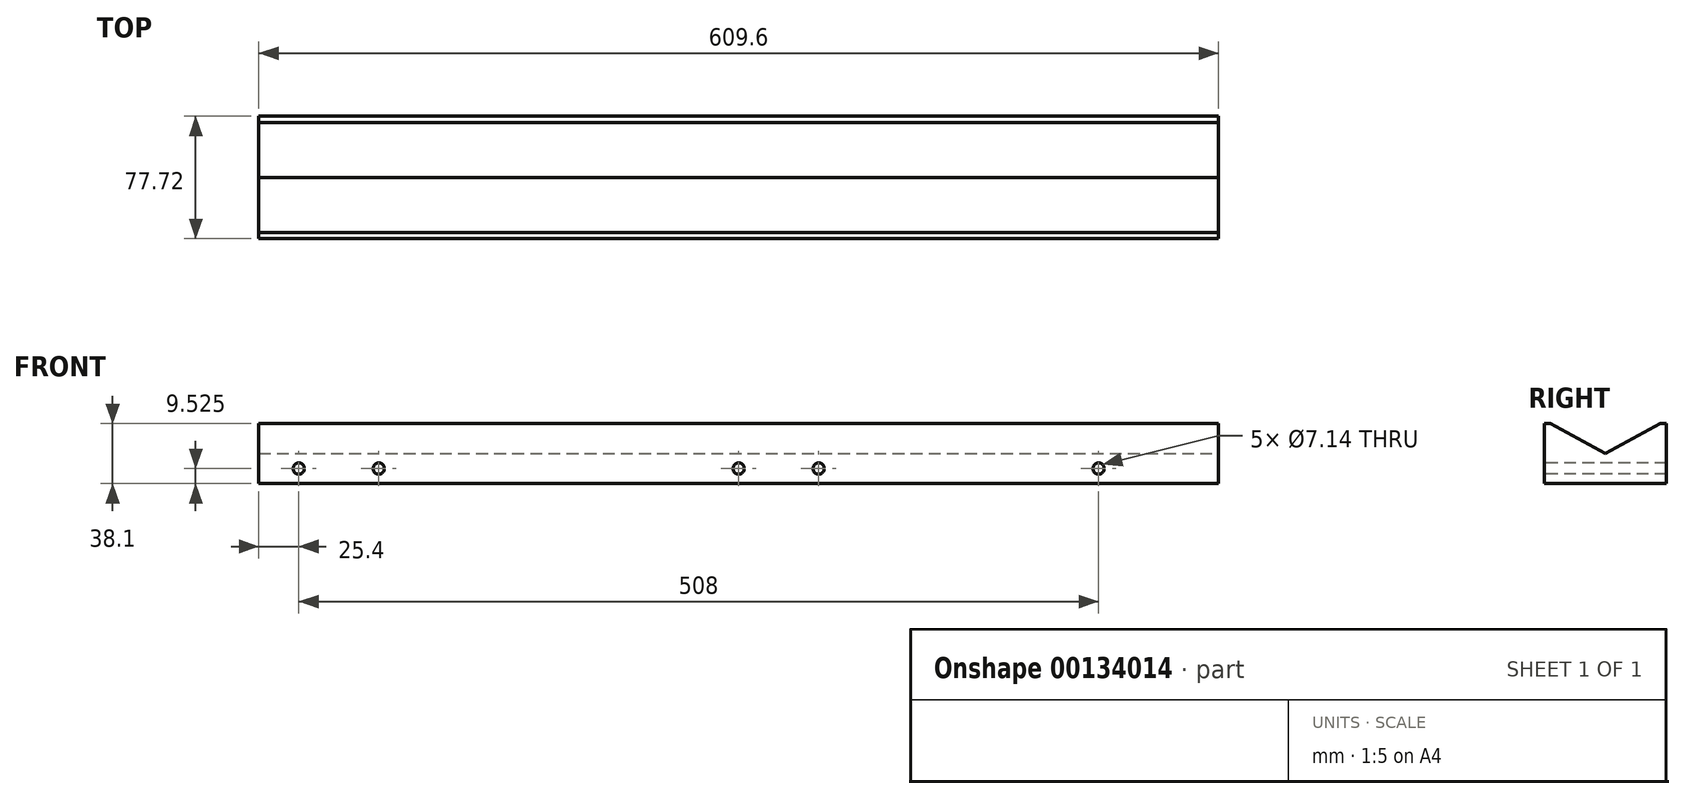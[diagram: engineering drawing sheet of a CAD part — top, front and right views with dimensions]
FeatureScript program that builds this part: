
annotation { "Feature Type Name" : "Feature", "Feature Type Description" : "" }
export const myFeature = defineFeature(function(context is Context, id is Id, definition is map)
    precondition{}
    {
        {
            var Q0;
            Q0=qCreatedBy(makeId("Right.planeOp"),FACE);
            var sketch = newSketch(context, id + "F0", { "sketchPlane" : qUnion([Q0])});
            skLineSegment(sketch, "E0.bottom", {"start": v(-38.86, 19.05) * mm, "end": v(38.86, 19.05) * mm});
            skLineSegment(sketch, "E0.top", {"start": v(-38.86, -19.05) * mm, "end": v(38.86, -19.05) * mm});
            skLineSegment(sketch, "E0.left", {"start": v(-38.86, 19.05) * mm, "end": v(-38.86, -19.05) * mm});
            skLineSegment(sketch, "E0.right", {"start": v(38.86, 19.05) * mm, "end": v(38.86, -19.05) * mm});
            skLineSegment(sketch, "E1", {"start": v(0, 19.05) * mm, "end": v(0, -19.05) * mm, "construction": true});
            skSolve(sketch);
        }
        {
            var Q0;
            Q0 = qSketchRegion(id + "F0", true);
            extrude(context, id + "F1", {"entities" : qUnion([Q0]), "endBound" : BoundingType.SYMMETRIC, "depth" : 609.6 * mm});
        }
        {
            var Q0;
            Q0=makeQuery(id+"F1.opExtrude","CAP_FACE",FACE,{"disambiguationData":[OSD([sQuery(id+"F0.wireOp",EDGE,"E0.bottom"),sQuery(id+"F0.wireOp",EDGE,"E0.top"),sQuery(id+"F0.wireOp",EDGE,"E0.left"),sQuery(id+"F0.wireOp",EDGE,"E0.right")])],"isStart":false});
            var sketch = newSketch(context, id + "F2", { "sketchPlane" : qUnion([Q0])});
            skLineSegment(sketch, "E2", {"start": v(-34.93, 19.05) * mm, "end": v(34.93, 19.05) * mm});
            skLineSegment(sketch, "E3", {"start": v(34.93, 19.05) * mm, "end": v(0, 0) * mm});
            skLineSegment(sketch, "E4", {"start": v(0, 0) * mm, "end": v(-34.93, 19.05) * mm});
            skLineSegment(sketch, "E5", {"start": v(0, 19.05) * mm, "end": v(0, 0) * mm, "construction": true});
            skSolve(sketch);
        }
        {
            var Q0;
            Q0 = qSketchRegion(id + "F2", true);
            extrude(context, id + "F3", {"entities" : qUnion([Q0]), "operationType" : NewBodyOperationType.REMOVE, "endBound" : BoundingType.THROUGH_ALL, "oppositeDirection" : true, "depth" : 25.4 * mm});
        }
        {
            var Q0;
            Q0=makeQuery(id+"F1.opExtrude","SWEPT_FACE",FACE,{"disambiguationData":[OSD([sQuery(id+"F0.wireOp",EDGE,"E0.left")])]});
            var sketch = newSketch(context, id + "F4", { "sketchPlane" : qUnion([Q0])});
            skLineSegment(sketch, "E6", {"start": v(-228.6, -9.53) * mm, "end": v(0, -9.53) * mm, "construction": true});
            skLineSegment(sketch, "E7", {"start": v(0, -9.53) * mm, "end": v(228.6, -9.53) * mm, "construction": true});
            skLineSegment(sketch, "E8", {"start": v(0, -19.05) * mm, "end": v(0, -9.53) * mm, "construction": true});
            skLineSegment(sketch, "E9", {"start": v(-228.6, -9.53) * mm, "end": v(-279.4, -9.53) * mm, "construction": true});
            skPoint(sketch, "E10", {"position": v(50.8, -9.53) * mm});
            skSolve(sketch);
        }
        {
            var Q0;
            Q0=sQuery(id+"F4.wireOp",VERTEX,"E6.start");
            var Q1;
            Q1=sQuery(id+"F4.wireOp",VERTEX,"E8.end");
            var Q2;
            Q2=sQuery(id+"F4.wireOp",VERTEX,"E7.end");
            var Q3;
            Q3=sQuery(id+"F4.wireOp",VERTEX,"E9.end");
            var Q4;
            Q4=sQuery(id+"F4.wireOp",VERTEX,"E10");
            var Q5;
            Q5=makeQuery(id+"F1.opExtrude","SWEPT_BODY",BODY,{"disambiguationData":[OSD([sQuery(id+"F0.wireOp",EDGE,"E0.bottom"),sQuery(id+"F0.wireOp",EDGE,"E0.top"),sQuery(id+"F0.wireOp",EDGE,"E0.left"),sQuery(id+"F0.wireOp",EDGE,"E0.right")])]});
            hole(context, id + "F5", {"style" : HoleStyle.SIMPLE, "endStyle" : HoleEndStyle.THROUGH, "holeDiameter" : 7.14 * mm, "locations" : qUnion([Q0, Q1, Q2, Q3, Q4]), "scope" : qUnion([Q5]), "isTappedThrough" : true});
        }
    });
